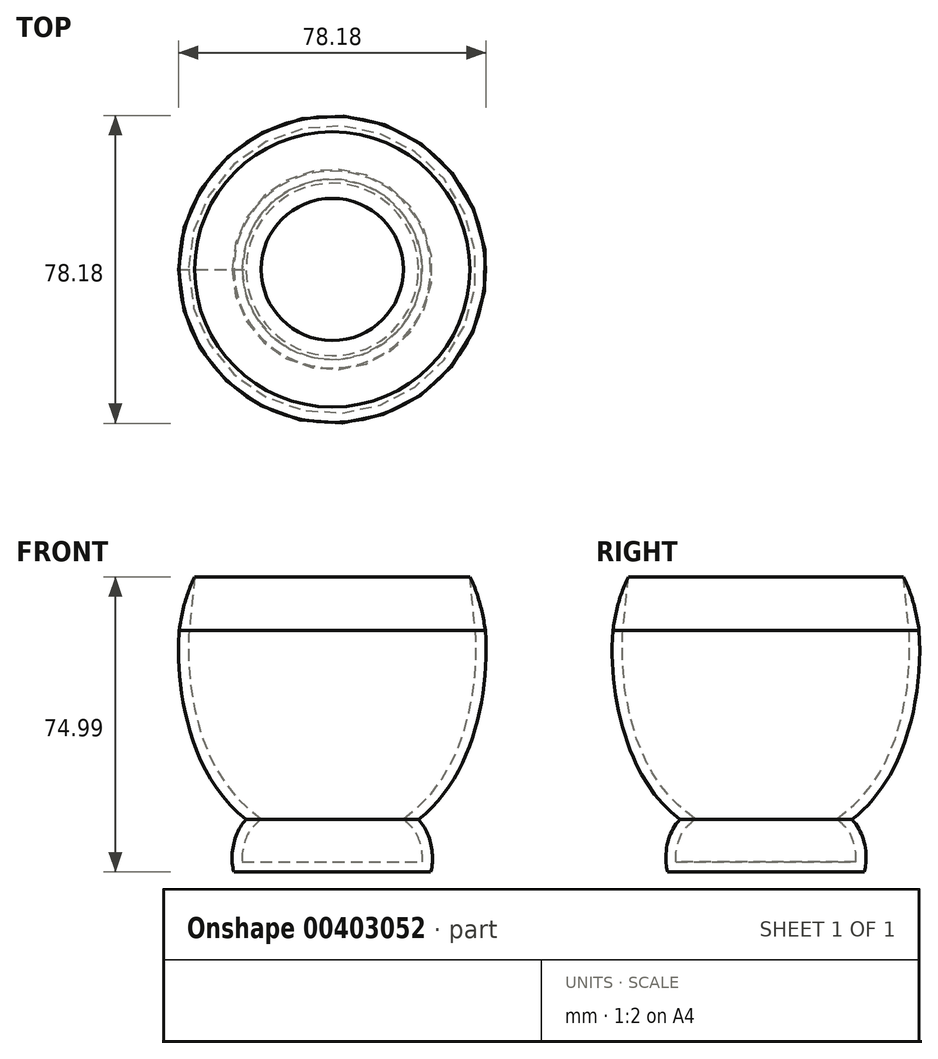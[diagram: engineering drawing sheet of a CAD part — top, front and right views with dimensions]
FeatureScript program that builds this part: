
annotation { "Feature Type Name" : "Feature", "Feature Type Description" : "" }
export const myFeature = defineFeature(function(context is Context, id is Id, definition is map)
    precondition{}
    {
        {
            var Q0;
            Q0=qCreatedBy(makeId("Front.planeOp"),FACE);
            var sketch = newSketch(context, id + "F0", { "sketchPlane" : qUnion([Q0])});
            skFitSpline(sketch, "E0", {"points": [v(-38.88, -6.55) * mm, v(-21.88, -54.61) * mm], "startDerivative": vector(-2.34, -23.45) * mm, "endDerivative": vector(51.58, -40.44) * mm});
            skFitSpline(sketch, "E1", {"points": [v(-21.88, -54.61) * mm, v(-25, -67.9) * mm], "startDerivative": vector(-9.38, -9.38) * mm, "endDerivative": vector(3.52, -12.3) * mm});
            skFitSpline(sketch, "E2", {"points": [v(-25, -67.9) * mm, v(0, -67.9) * mm], "startDerivative": vector(25, 0) * mm, "endDerivative": vector(25, 0) * mm});
            skLineSegment(sketch, "E3", {"start": v(0, -67.9) * mm, "end": v(0, 21.74) * mm});
            skFitSpline(sketch, "E4", {"points": [v(-38.88, -6.55) * mm, v(-22.49, 19.47) * mm, v(0, 21.74) * mm], "startDerivative": vector(11.07, 81.58) * mm, "endDerivative": vector(52.51, 0) * mm});
            skSolve(sketch);
        }
        {
            var Q0;
            Q0=makeQuery(id+"F0.imprint","IMPRINT",FACE,{"disambiguationData":[TD([[makeQuery(id+"F0.imprint","IMPRINT",EDGE,{"derivedFrom":sQuery(id+"F0.wireOp",EDGE,"E0")}),1.0]])]});
            var Q1;
            Q1=sQuery(id+"F0.wireOp",EDGE,"E3");
            revolve(context, id + "F1", {"entities" : qUnion([Q0]), "axis" : qUnion([Q1]), "revolveType" : RevolveType.FULL});
        }
        {
            var Q0;
            Q0=makeQuery(id+"F1.opRevolve","SWEPT_FACE",FACE,{"disambiguationData":[OSD([sQuery(id+"F0.wireOp",EDGE,"E4")])]});
            shell(context, id + "F2", {"entities" : qUnion([Q0]), "thickness" : 2.54 * mm});
        }
        {
            var Q0;
            Q0=qCreatedBy(makeId("Front.planeOp"),FACE);
            cPlane(context, id + "F3", {"entities" : qUnion([Q0]), "cplaneType" : CPlaneType.OFFSET, "offset" : 0 * mm, "width" : 152.4 * mm, "height" : 152.4 * mm});
        }
        {
            var Q0;
            Q0=qCreatedBy(makeId("Right.planeOp"),FACE);
            cPlane(context, id + "F4", {"entities" : qUnion([Q0]), "cplaneType" : CPlaneType.OFFSET, "offset" : 25.4 * mm, "width" : 152.4 * mm, "height" : 152.4 * mm});
        }
    });
